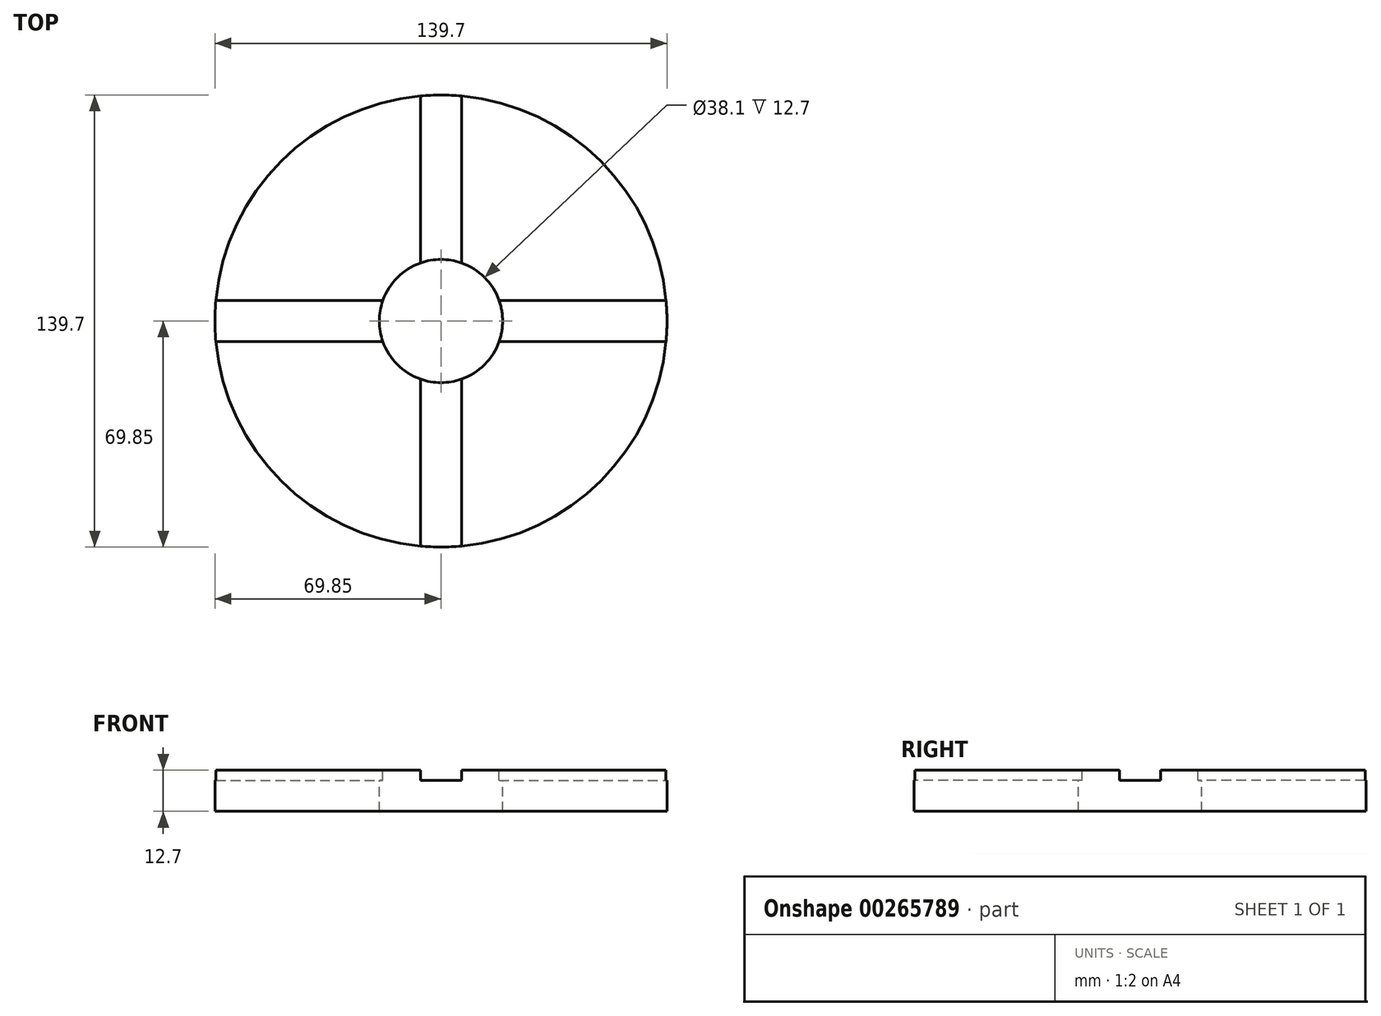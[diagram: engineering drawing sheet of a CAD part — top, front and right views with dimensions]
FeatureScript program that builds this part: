
annotation { "Feature Type Name" : "Feature", "Feature Type Description" : "" }
export const myFeature = defineFeature(function(context is Context, id is Id, definition is map)
    precondition{}
    {
        {
            var Q0;
            Q0=qCreatedBy(makeId("Top.planeOp"),FACE);
            var sketch = newSketch(context, id + "F0", { "sketchPlane" : qUnion([Q0])});
            skCircle(sketch, "E0", {"center": v(0, 0) * mm, "radius": 69.85 * mm});
            skSolve(sketch);
        }
        {
            var Q0;
            Q0 = qSketchRegion(id + "F0", true);
            extrude(context, id + "F1", {"entities" : qUnion([Q0]), "oppositeDirection" : true, "depth" : 12.7 * mm});
        }
        {
            var Q0;
            Q0=qCreatedBy(makeId("Top.planeOp"),FACE);
            var sketch = newSketch(context, id + "F2", { "sketchPlane" : qUnion([Q0])});
            skLineSegment(sketch, "E1.0", {"start": v(-6.35, 76.04) * mm, "end": v(-6.35, 6.35) * mm});
            skLineSegment(sketch, "E2.0", {"start": v(6.35, 76.04) * mm, "end": v(6.35, 6.35) * mm});
            skLineSegment(sketch, "E3.0", {"start": v(-75.38, -6.35) * mm, "end": v(-6.35, -6.35) * mm});
            skLineSegment(sketch, "E4.0", {"start": v(-75.38, 6.35) * mm, "end": v(-6.35, 6.35) * mm});
            skLineSegment(sketch, "E5", {"start": v(-6.35, 76.04) * mm, "end": v(6.35, 76.04) * mm});
            skLineSegment(sketch, "E6", {"start": v(-75.38, -6.35) * mm, "end": v(-75.38, 6.35) * mm});
            skLineSegment(sketch, "E7", {"start": v(-6.35, -74.06) * mm, "end": v(6.35, -74.06) * mm});
            skLineSegment(sketch, "E8", {"start": v(76.04, -6.35) * mm, "end": v(76.04, 6.35) * mm});
            skLineSegment(sketch, "E9.trimOffspring", {"start": v(6.35, 6.35) * mm, "end": v(76.04, 6.35) * mm});
            skLineSegment(sketch, "E10.trimOffspring", {"start": v(6.35, -6.35) * mm, "end": v(76.04, -6.35) * mm});
            skLineSegment(sketch, "E11.trimOffspring", {"start": v(-6.35, -6.35) * mm, "end": v(-6.35, -74.06) * mm});
            skLineSegment(sketch, "E12.trimOffspring", {"start": v(6.35, -6.35) * mm, "end": v(6.35, -74.06) * mm});
            skSolve(sketch);
        }
        {
            var Q0;
            Q0 = qSketchRegion(id + "F2", true);
            extrude(context, id + "F3", {"entities" : qUnion([Q0]), "operationType" : NewBodyOperationType.REMOVE, "oppositeDirection" : true, "depth" : 3.17 * mm});
        }
        {
            var Q0;
            Q0=qCreatedBy(makeId("Top.planeOp"),FACE);
            var sketch = newSketch(context, id + "F4", { "sketchPlane" : qUnion([Q0])});
            skCircle(sketch, "E13", {"center": v(0, 0) * mm, "radius": 19.05 * mm});
            skSolve(sketch);
        }
        {
            var Q0;
            Q0 = qSketchRegion(id + "F4", true);
            extrude(context, id + "F5", {"entities" : qUnion([Q0]), "operationType" : NewBodyOperationType.REMOVE, "endBound" : BoundingType.THROUGH_ALL, "oppositeDirection" : true, "depth" : 25.4 * mm});
        }
    });
